# Revit family: Clevertronics_ARGO-600-SEN-LP
name_source: partatom
category: Lighting Fixtures
units: mm (PartAtom-declared; Revit-internal decimal feet)

## family parameters
Cut with Voids When Loaded = No
Host = Face
Light Source = Yes
Part Type = Normal
Room Calculation Point = No
Round Connector Dimension = Use Diameter
Shared = No

## types (5) — shared parameters
Apparent Load = 20 VA
Clevertronics_240V Driver = 1330087-A 240V Driver
Clevertronics_240V LED Strip = 8002848 LED Strip
Clevertronics_AS2293 Classification = C0=D40 C90=D25
Clevertronics_Applicable Standards = AS/NZS3820, CISPR15, AS/NZS2293.3
Clevertronics_Battery = 3.2V 3200mAh
Clevertronics_Battery Type = Lithium Iron Phosphate
Clevertronics_Charger Method = Intelligent current limited constant voltage
Clevertronics_Construction = Polycarbonate Base and Diffuser with Captive Stainless-Steel Clips (SS301)
Clevertronics_Diffuser = Polycarbonate
Clevertronics_Driver/Ballast = LED Driver – 20w Stallion, MS-HL
Clevertronics_Height = 88 mm  [stored 0.288714 ft]
Clevertronics_IK Rating = IK08
Clevertronics_IP Rating = IP65
Clevertronics_Length = 655 mm  [stored 2.14895 ft]
Clevertronics_Material = Clevertronics_Plycarbonate Base
Clevertronics_Mounting = Surface mount
Clevertronics_Operating Mode = Sustained
Clevertronics_Operating Temperature = 0˚C to 40˚C
Clevertronics_Operating Voltage = 240V AC; 50Hz
Clevertronics_Power Consumption = 22W
Clevertronics_Replacement Battery = 1550050 Battery
Clevertronics_Weight = 1.5 kg
Clevertronics_Width = 121 mm  [stored 0.396982 ft]
Color Filter = 16777215
Default Elevation = 1200 mm
Dimming Lamp Color Temperature Shift = <None>
Lamp = Dual LED strip module, 3,000K warm white, 5,700K cool white,
50,000h life [L70/B50 Ta 40°C], Ra>80
Manufacturer = Clevertronics
Photometric Web File = ARGO-600-SEN-LP_IESR_E_693-7_20200803-01.ies
Tilt Angle = -90.00°
zero-valued in all types: Clevertronics_Annotation Size

## per-type parameters (varying)
| type | Clevertronics_Emergency Driver | Clevertronics_MIC Number | Clevertronics_Product Description | Clevertronics_Testing Node | Clevertronics_Testing System | Description | Model |
| ARGO-600-SEN-LP AUB02320460001 | AUM02370080001 CLIFE-PRO-CKIT-NP-335 Driver Pack | AUB02320460001 | LP Premium ARGO 600mm LED Weatherproof Emergency Batten with Integral Battery, Microwave Sensor (Hi/Lo) and Switchable Colour, Enabled with Clevertest Plus |  | Clevertest Plus Enabled (Not activated by default) | LP Premium ARGO 600mm LED Weatherproof Emergency Batten 
with Integral Battery, Microwave Sensor (Hi/Lo) and Switchable Colour, 
Enabled with Clevertest Plus | ARGO-600-SEN-LP |
| ARGO-600-SEN-LP-HV AUB02820550001 | AUM02870060001 CLIFE-PRO-CKIT-HV-NP-335 Driver Pack | AUB02820550001 | LP Premium ARGO 600mm LED Weatherproof Emergency Batten with Integral Battery, Microwave Sensor (Hi/Lo) and Switchable Colour | 8003191 Communications Node - HV | Zoneworks XT HIVE (RF) | LP Premium ARGO 600mm LED Weatherproof Emergency Batten 
with Integral Battery, Microwave Sensor (Hi/Lo) and Switchable Colour | ARGO-600-SEN-LP-HV |
| ARGO-600-SEN-LP-DALI AUB02221220002 | AUM02270290002 CLIFE-PRO-CKIT-DALI-NP-335 Driver Pack | AUB02221220002 | Argo 600mm Weatherproof Emergency Batten, LP, Switchable Colour, Motion 
Sensor, Zoneworks XT Hive 2.4GHz | 8003060 Communications Node - DALI | DALI Registered | LP Premium ARGO 600mm LED Weatherproof Emergency Batten 
with Integral Battery, Microwave Sensor (Hi/Lo) and Switchable Colour, 
Enabled with Clevertest Plus | ARGO-600-SEN-LP-DALI |
| ARGO-600-SEN-LP-HVG AUB02920140001 | AUM02970070002 CLIFE-PRO-CKIT-HVG-NP-335 Driver Pack | AUB02920140001 | LP Premium ARGO 600mm LED Weatherproof Emergency Batten with Integral Battery, Microwave Sensor (Hi/Lo) and Switchable Colour | 8003560 Communications Node - HVG | Zoneworks XT HIVE (RF) | Argo 600mm Weatherproof Emergency Batten, LP, Switchable Colour, Motion 
Sensor, Zoneworks XT Hive 2.4GHz | ARGO-600-SEN-LP-HVG |
| ARGO-600-SEN-LP-ZW AUB02120400001 | AUM02170030001 CLIFE-PRO-CKIT-ZW-NP-335 Driver Pack | AUB02120400001 | LP Premium ARGO 600mm LED Weatherproof Emergency Batten with Integral Battery, Microwave Sensor (Hi/Lo) and Switchable Colour | 8001450 Communications Node - ZW | Zoneworks Computerised Testing | LP Premium ARGO 600mm LED Weatherproof Emergency Batten 
with Integral Battery, Microwave Sensor (Hi/Lo) and Switchable Colour, 
Enabled with Clevertest Plus | ARGO-600-SEN-LP-ZW |

note: [stored X ft] marks values corroborated as IEEE doubles in the binary element streams (Revit-internal decimal feet)

## geometry (parser evidence)
native form markers: Blend x2, Sweep x3
no freeform markers — native parametric forms only
